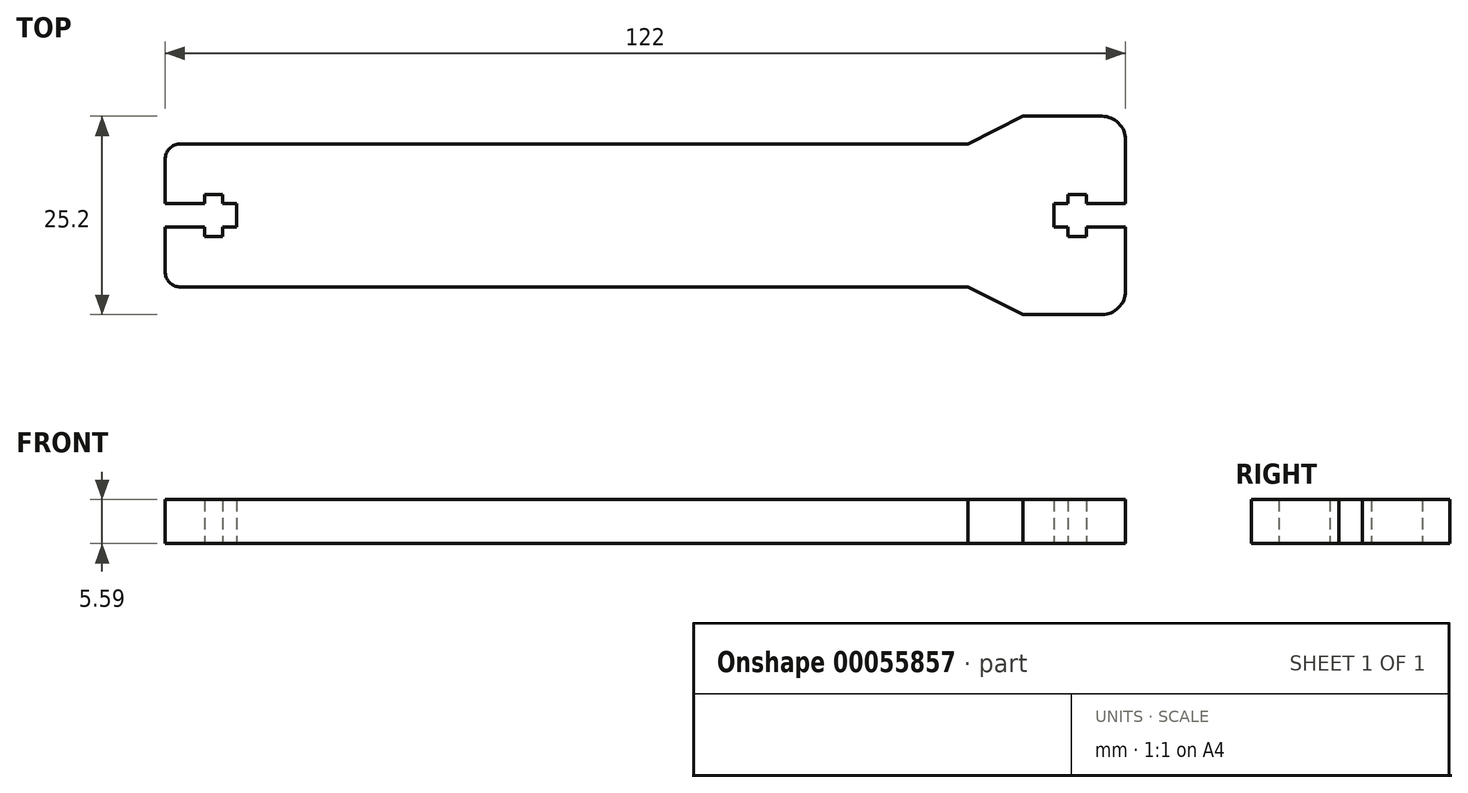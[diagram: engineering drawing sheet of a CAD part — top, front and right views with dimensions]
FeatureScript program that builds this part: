
annotation { "Feature Type Name" : "Feature", "Feature Type Description" : "" }
export const myFeature = defineFeature(function(context is Context, id is Id, definition is map)
    precondition{}
    {
        {
            var Q0;
            Q0=qCreatedBy(makeId("Top.planeOp"),FACE);
            var sketch = newSketch(context, id + "F0", { "sketchPlane" : qUnion([Q0])});
            skLineSegment(sketch, "E0.bottom", {"start": v(-59, 9.1) * mm, "end": v(61, 9.1) * mm});
            skLineSegment(sketch, "E0.top", {"start": v(-59, -9.1) * mm, "end": v(61, -9.1) * mm});
            skLineSegment(sketch, "E1", {"start": v(-61, 7.1) * mm, "end": v(-61, 1.5) * mm});
            skLineSegment(sketch, "E2", {"start": v(-61, -7.1) * mm, "end": v(-61, -1.5) * mm});
            skLineSegment(sketch, "E3", {"start": v(-61, 1.5) * mm, "end": v(-56, 1.5) * mm});
            skLineSegment(sketch, "E4", {"start": v(-61, -1.5) * mm, "end": v(-56, -1.5) * mm});
            skLineSegment(sketch, "E5", {"start": v(-56, 1.5) * mm, "end": v(-56, 2.65) * mm});
            skLineSegment(sketch, "E6", {"start": v(-56, 2.65) * mm, "end": v(-53.7, 2.65) * mm});
            skLineSegment(sketch, "E7", {"start": v(-53.7, 2.65) * mm, "end": v(-53.7, 1.5) * mm});
            skLineSegment(sketch, "E8", {"start": v(-53.7, 1.5) * mm, "end": v(-51.93, 1.5) * mm});
            skLineSegment(sketch, "E9", {"start": v(-51.93, 1.5) * mm, "end": v(-51.93, -1.5) * mm});
            skLineSegment(sketch, "E10", {"start": v(-51.93, -1.5) * mm, "end": v(-53.7, -1.5) * mm});
            skLineSegment(sketch, "E11", {"start": v(-53.7, -1.5) * mm, "end": v(-53.7, -2.65) * mm});
            skLineSegment(sketch, "E12", {"start": v(-56, -1.5) * mm, "end": v(-56, -2.65) * mm});
            skLineSegment(sketch, "E13", {"start": v(-56, -2.65) * mm, "end": v(-53.7, -2.65) * mm});
            skPoint(sketch, "E14.visualSharp", {"position": v(-61, 9.1) * mm});
            skArc(sketch, "E14.filletArc", {"start": v(-59, 9.1) * mm, "mid": v(-60.41, 8.51) * mm, "end": v(-61, 7.1) * mm});
            skPoint(sketch, "E15.visualSharp", {"position": v(-61, -9.1) * mm});
            skArc(sketch, "E15.filletArc", {"start": v(-61, -7.1) * mm, "mid": v(-60.41, -8.51) * mm, "end": v(-59, -9.1) * mm});
            skLineSegment(sketch, "E16.MirrorCS", {"start": v(56, -2.65) * mm, "end": v(53.7, -2.65) * mm});
            skLineSegment(sketch, "E17.MirrorCS", {"start": v(56, -1.5) * mm, "end": v(56, -2.65) * mm});
            skLineSegment(sketch, "E18.MirrorCS", {"start": v(53.7, -1.5) * mm, "end": v(53.7, -2.65) * mm});
            skLineSegment(sketch, "E19.MirrorCS", {"start": v(51.93, 1.5) * mm, "end": v(51.93, -1.5) * mm});
            skLineSegment(sketch, "E20.MirrorCS", {"start": v(51.93, -1.5) * mm, "end": v(53.7, -1.5) * mm});
            skLineSegment(sketch, "E21.MirrorCS", {"start": v(53.7, 1.5) * mm, "end": v(51.93, 1.5) * mm});
            skLineSegment(sketch, "E22.MirrorCS", {"start": v(53.7, 2.65) * mm, "end": v(53.7, 1.5) * mm});
            skLineSegment(sketch, "E23.MirrorCS", {"start": v(56, 2.65) * mm, "end": v(53.7, 2.65) * mm});
            skLineSegment(sketch, "E24.MirrorCS", {"start": v(56, 1.5) * mm, "end": v(56, 2.65) * mm});
            skLineSegment(sketch, "E25.MirrorCS", {"start": v(61, -1.5) * mm, "end": v(56, -1.5) * mm});
            skPoint(sketch, "E26.MirrorP", {"position": v(61, -9.1) * mm});
            skLineSegment(sketch, "E27.MirrorCS", {"start": v(61, 7.1) * mm, "end": v(61, 1.5) * mm});
            skLineSegment(sketch, "E28.MirrorCS", {"start": v(61, -7.1) * mm, "end": v(61, -1.5) * mm});
            skLineSegment(sketch, "E29.MirrorCS", {"start": v(61, 1.5) * mm, "end": v(56, 1.5) * mm});
            skLineSegment(sketch, "E30", {"start": v(61, -9.1) * mm, "end": v(61, -7.1) * mm});
            skLineSegment(sketch, "E31", {"start": v(61, 9.1) * mm, "end": v(61, 7.1) * mm});
            skSolve(sketch);
        }
        {
            var Q0;
            Q0 = qSketchRegion(id + "F0", true);
            extrude(context, id + "F1", {"entities" : qUnion([Q0]), "depth" : 5.6 * mm});
        }
        {
            var Q0;
            Q0=makeQuery(id+"F1.opExtrude","SWEPT_FACE",FACE,{"disambiguationData":[OSD([sQuery(id+"F0.wireOp",EDGE,"E0.bottom")])]});
            var sketch = newSketch(context, id + "F2", { "sketchPlane" : qUnion([Q0])});
            skLineSegment(sketch, "E32.bottom", {"start": v(-61, 5.59) * mm, "end": v(-41, 5.59) * mm});
            skLineSegment(sketch, "E32.top", {"start": v(-61, 0) * mm, "end": v(-41, 0) * mm});
            skLineSegment(sketch, "E32.left", {"start": v(-61, 5.59) * mm, "end": v(-61, 0) * mm});
            skLineSegment(sketch, "E32.right", {"start": v(-41, 5.59) * mm, "end": v(-41, 0) * mm});
            skSolve(sketch);
        }
        {
            var Q0;
            Q0 = qSketchRegion(id + "F2", true);
            extrude(context, id + "F3", {"entities" : qUnion([Q0]), "operationType" : NewBodyOperationType.ADD, "depth" : 3.5 * mm});
        }
        {
            var Q0;
            Q0=makeQuery(id+"F3.opExtrude","CAP_EDGE",EDGE,{"disambiguationData":[OSD([sQuery(id+"F2.wireOp",EDGE,"E32.right")])],"isStart":false});
            chamfer(context, id + "F4", {"entities" : qUnion([Q0]), "chamferType" : ChamferType.TWO_OFFSETS, "width1" : 3.5 * mm, "oppositeDirection" : false, "width2" : 7 * mm, "tangentPropagation" : true});
        }
        {
            var Q0;
            Q0=makeQuery(id+"F1.opExtrude","SWEPT_FACE",FACE,{"disambiguationData":[OSD([sQuery(id+"F0.wireOp",EDGE,"E0.top")])]});
            var sketch = newSketch(context, id + "F5", { "sketchPlane" : qUnion([Q0])});
            skLineSegment(sketch, "E33.bottom", {"start": v(61, 5.59) * mm, "end": v(41, 5.59) * mm});
            skLineSegment(sketch, "E33.top", {"start": v(61, 0) * mm, "end": v(41, 0) * mm});
            skLineSegment(sketch, "E33.left", {"start": v(61, 5.59) * mm, "end": v(61, 0) * mm});
            skLineSegment(sketch, "E33.right", {"start": v(41, 5.59) * mm, "end": v(41, 0) * mm});
            skSolve(sketch);
        }
        {
            var Q0;
            Q0 = qSketchRegion(id + "F5", true);
            extrude(context, id + "F6", {"entities" : qUnion([Q0]), "operationType" : NewBodyOperationType.ADD, "depth" : 3.5 * mm});
        }
        {
            var Q0;
            Q0=makeQuery(id+"F6.opExtrude","CAP_EDGE",EDGE,{"disambiguationData":[OSD([sQuery(id+"F5.wireOp",EDGE,"E33.right")])],"isStart":false});
            chamfer(context, id + "F7", {"entities" : qUnion([Q0]), "chamferType" : ChamferType.TWO_OFFSETS, "width1" : 7 * mm, "oppositeDirection" : false, "width2" : 3.5 * mm, "tangentPropagation" : true});
        }
        {
            var Q0;
            Q0=makeQuery(id+"F3.opExtrude","CAP_EDGE",EDGE,{"disambiguationData":[OSD([sQuery(id+"F2.wireOp",EDGE,"E32.left")])],"isStart":false});
            var Q1;
            Q1=makeQuery(id+"F6.opExtrude","CAP_EDGE",EDGE,{"disambiguationData":[OSD([sQuery(id+"F5.wireOp",EDGE,"E33.left")])],"isStart":false});
            fillet(context, id + "F8", {"entities" : qUnion([Q0, Q1]), "radius" : 3 * mm, "tangentPropagation" : true, "allowEdgeOverflow" : false});
        }
    });
